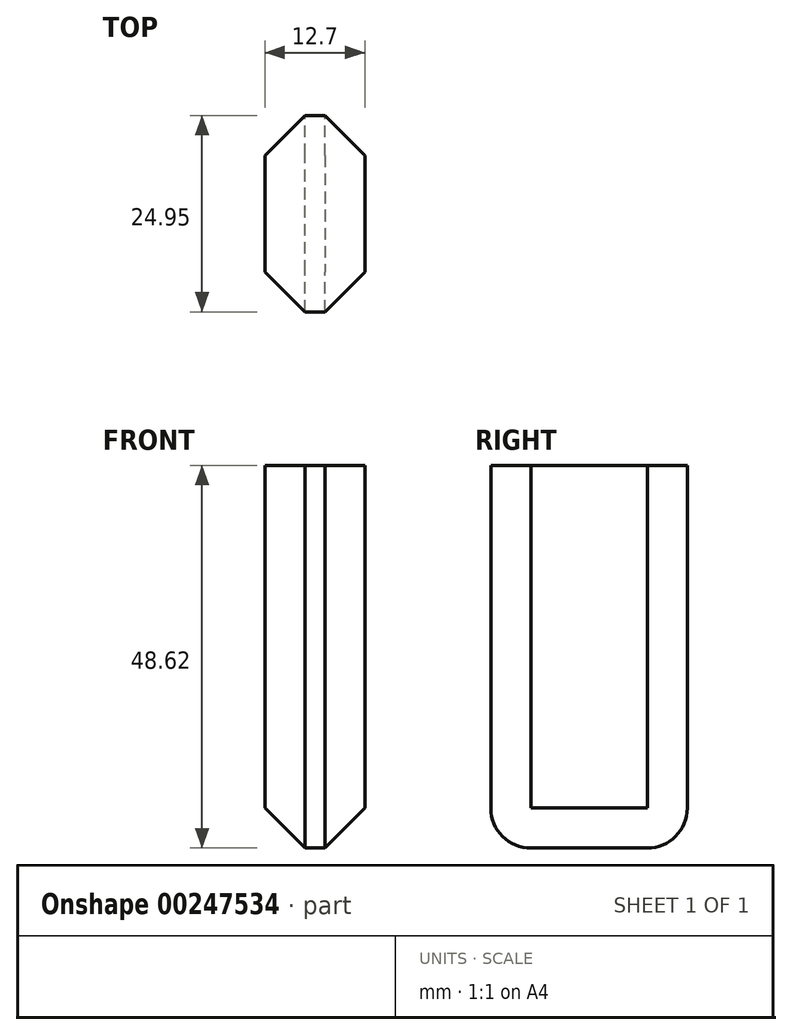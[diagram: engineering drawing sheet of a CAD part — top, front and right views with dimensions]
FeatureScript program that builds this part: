
annotation { "Feature Type Name" : "Feature", "Feature Type Description" : "" }
export const myFeature = defineFeature(function(context is Context, id is Id, definition is map)
    precondition{}
    {
        {
            var Q0;
            Q0=qCreatedBy(makeId("Right.planeOp"),FACE);
            var sketch = newSketch(context, id + "F0", { "sketchPlane" : qUnion([Q0])});
            skLineSegment(sketch, "E0.bottom", {"start": v(-15.7, 33.96) * mm, "end": v(9.26, 33.96) * mm});
            skLineSegment(sketch, "E0.top", {"start": v(-15.7, -14.66) * mm, "end": v(9.26, -14.66) * mm});
            skLineSegment(sketch, "E0.left", {"start": v(-15.7, 33.96) * mm, "end": v(-15.7, -14.66) * mm});
            skLineSegment(sketch, "E0.right", {"start": v(9.26, 33.96) * mm, "end": v(9.26, -14.66) * mm});
            skSolve(sketch);
        }
        {
            var Q0;
            Q0 = qSketchRegion(id + "F0", true);
            extrude(context, id + "F1", {"entities" : qUnion([Q0]), "depth" : 12.7 * mm});
        }
        {
            var Q0;
            Q0=makeQuery(id+"F1.opExtrude","SWEPT_EDGE",EDGE,{"disambiguationData":[OSD([sQuery(id+"F0.wireOp",EDGE,"E0.top"),sQuery(id+"F0.wireOp",EDGE,"E0.left")])]});
            var Q1;
            Q1=makeQuery(id+"F1.opExtrude","SWEPT_EDGE",EDGE,{"disambiguationData":[OSD([sQuery(id+"F0.wireOp",EDGE,"E0.top"),sQuery(id+"F0.wireOp",EDGE,"E0.right")])]});
            fillet(context, id + "F2", {"entities" : qUnion([Q0, Q1]), "radius" : 5.08 * mm, "tangentPropagation" : true, "allowEdgeOverflow" : false});
        }
        {
            var Q0;
            Q0=makeQuery(id+"F1.opExtrude","CAP_EDGE",EDGE,{"disambiguationData":[OSD([sQuery(id+"F0.wireOp",EDGE,"E0.top")])],"isStart":false});
            var Q1;
            Q1=makeQuery(id+"F1.opExtrude","CAP_EDGE",EDGE,{"disambiguationData":[OSD([sQuery(id+"F0.wireOp",EDGE,"E0.top")])],"isStart":true});
            chamfer(context, id + "F3", {"entities" : qUnion([Q0, Q1]), "width" : 5.08 * mm, "tangentPropagation" : true});
        }
    });
